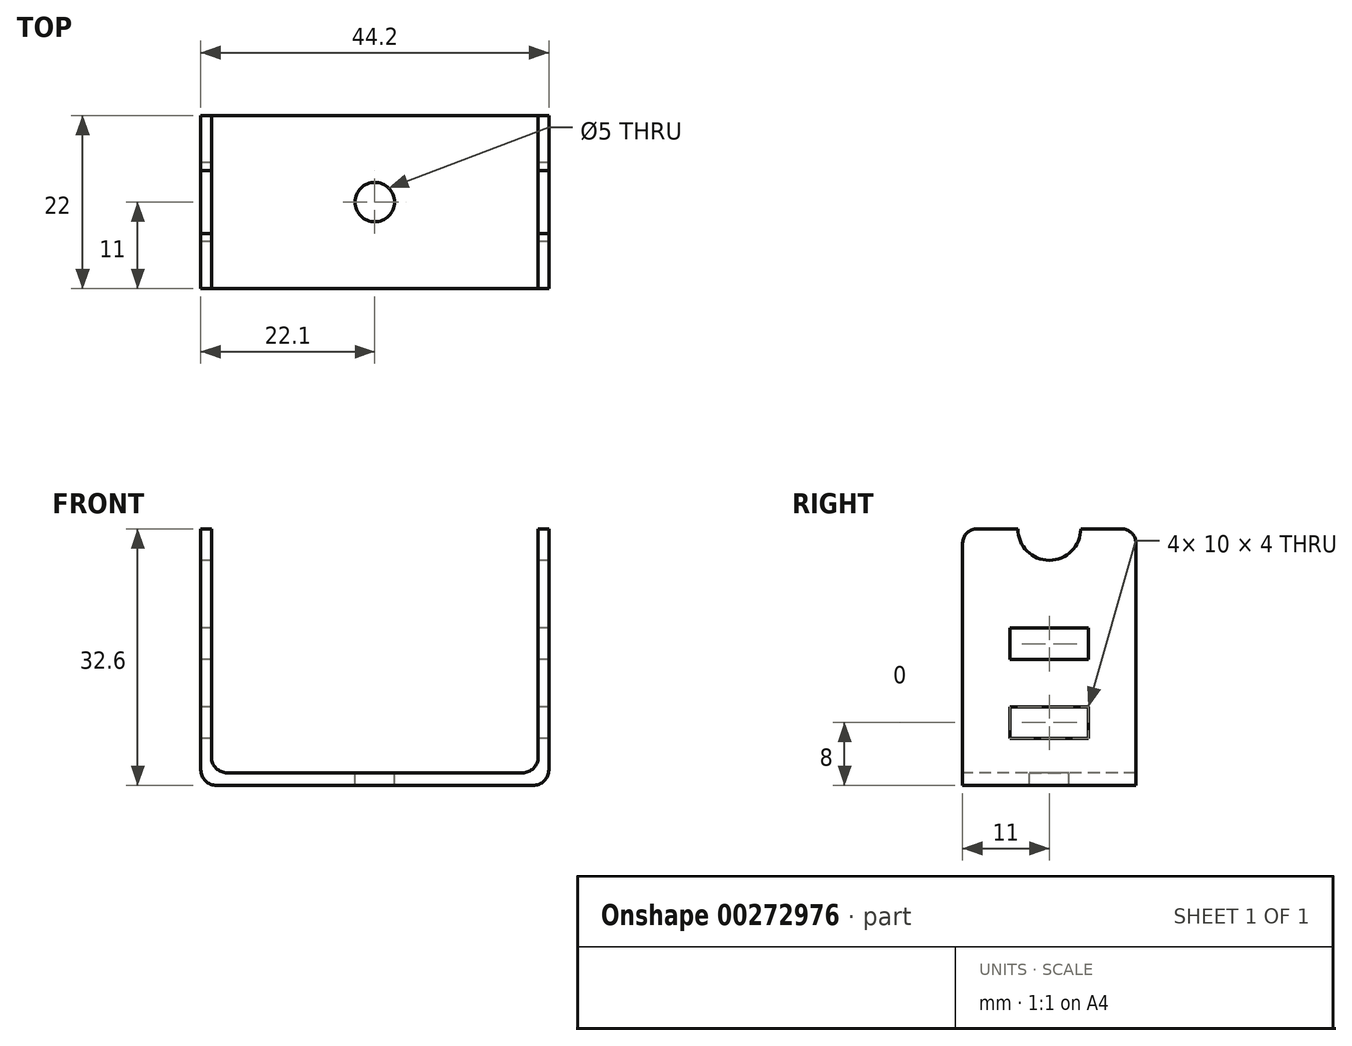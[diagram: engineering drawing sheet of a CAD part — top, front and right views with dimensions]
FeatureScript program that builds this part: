
annotation { "Feature Type Name" : "Feature", "Feature Type Description" : "" }
export const myFeature = defineFeature(function(context is Context, id is Id, definition is map)
    precondition{}
    {
        {
            var Q0;
            Q0=qCreatedBy(makeId("Right.planeOp"),FACE);
            var sketch = newSketch(context, id + "F0", { "sketchPlane" : qUnion([Q0])});
            skLineSegment(sketch, "E0.bottom", {"start": v(-11, 0) * mm, "end": v(11, 0) * mm});
            skLineSegment(sketch, "E0.top", {"start": v(-9.17, 32.6) * mm, "end": v(-4, 32.6) * mm});
            skLineSegment(sketch, "E0.left", {"start": v(-11, 0) * mm, "end": v(-11, 30.77) * mm});
            skLineSegment(sketch, "E0.right", {"start": v(11, 0) * mm, "end": v(11, 30.77) * mm});
            skLineSegment(sketch, "E1.bottom", {"start": v(-5, 10) * mm, "end": v(5, 10) * mm});
            skLineSegment(sketch, "E1.top", {"start": v(-5, 6) * mm, "end": v(5, 6) * mm});
            skLineSegment(sketch, "E1.left", {"start": v(-5, 10) * mm, "end": v(-5, 6) * mm});
            skLineSegment(sketch, "E1.right", {"start": v(5, 10) * mm, "end": v(5, 6) * mm});
            skLineSegment(sketch, "E2.0.1.0", {"start": v(-5, 16) * mm, "end": v(5, 16) * mm});
            skLineSegment(sketch, "E2.0.1.1", {"start": v(5, 20) * mm, "end": v(5, 16) * mm});
            skLineSegment(sketch, "E2.0.1.2", {"start": v(-5, 20) * mm, "end": v(5, 20) * mm});
            skLineSegment(sketch, "E2.0.1.3", {"start": v(-5, 20) * mm, "end": v(-5, 16) * mm});
            skLineSegment(sketch, "E2.direction1", {"start": v(-5, 6) * mm, "end": v(17, 6) * mm, "construction": true});
            skLineSegment(sketch, "E2.direction2", {"start": v(-5, 6) * mm, "end": v(-5, 16) * mm, "construction": true});
            skArc(sketch, "E3", {"start": v(-4, 32.6) * mm, "mid": v(0, 28.6) * mm, "end": v(4, 32.6) * mm});
            skLineSegment(sketch, "E4.trimOffspring", {"start": v(4, 32.6) * mm, "end": v(9.17, 32.6) * mm});
            skPoint(sketch, "E5.visualSharp", {"position": v(-11, 32.6) * mm});
            skArc(sketch, "E5.filletArc", {"start": v(-9.17, 32.6) * mm, "mid": v(-10.46, 32.06) * mm, "end": v(-11, 30.77) * mm});
            skPoint(sketch, "E6.visualSharp", {"position": v(11, 32.6) * mm});
            skArc(sketch, "E6.filletArc", {"start": v(11, 30.77) * mm, "mid": v(10.46, 32.06) * mm, "end": v(9.17, 32.6) * mm});
            skSolve(sketch);
        }
        {
            var Q0;
            Q0 = qSketchRegion(id + "F0", true);
            extrude(context, id + "F1", {"entities" : qUnion([Q0]), "endBound" : BoundingType.SYMMETRIC, "depth" : 44.2 * mm});
        }
        {
            var Q0;
            Q0=makeQuery(id+"F1.opExtrude","SWEPT_FACE",FACE,{"disambiguationData":[OSD([sQuery(id+"F0.wireOp",EDGE,"E0.top")])]});
            var sketch = newSketch(context, id + "F2", { "sketchPlane" : qUnion([Q0])});
            skLineSegment(sketch, "E7.bottom", {"start": v(-20.75, 21.18) * mm, "end": v(20.75, 21.18) * mm});
            skLineSegment(sketch, "E7.top", {"start": v(-20.75, -22.3) * mm, "end": v(20.75, -22.3) * mm});
            skLineSegment(sketch, "E7.left", {"start": v(-20.75, 21.18) * mm, "end": v(-20.75, -22.3) * mm});
            skLineSegment(sketch, "E7.right", {"start": v(20.75, 21.18) * mm, "end": v(20.75, -22.3) * mm});
            skSolve(sketch);
        }
        {
            var Q0;
            Q0 = qSketchRegion(id + "F2", true);
            extrude(context, id + "F3", {"entities" : qUnion([Q0]), "operationType" : NewBodyOperationType.REMOVE, "oppositeDirection" : true, "depth" : (32.5 - 1.5) * mm});
        }
        {
            var Q0;
            Q0=makeQuery(id+"F1.opExtrude","CAP_EDGE",EDGE,{"disambiguationData":[OSD([sQuery(id+"F0.wireOp",EDGE,"E0.bottom")])],"isStart":true});
            fillet(context, id + "F4", {"entities" : qUnion([Q0]), "radius" : 2 * mm, "tangentPropagation" : true, "allowEdgeOverflow" : false});
        }
        {
            var Q0;
            Q0=makeQuery(id+"F1.opExtrude","CAP_EDGE",EDGE,{"disambiguationData":[OSD([sQuery(id+"F0.wireOp",EDGE,"E0.bottom")])],"isStart":false});
            var Q1;
            Q1=makeQuery(id+"F3.boolean.opBoolean","COPY",EDGE,{"derivedFrom":makeQuery(id+"F3.opExtrude","CAP_EDGE",EDGE,{"disambiguationData":[OSD([sQuery(id+"F2.wireOp",EDGE,"E7.left")])],"isStart":false})});
            var Q2;
            Q2=makeQuery(id+"F3.boolean.opBoolean","COPY",EDGE,{"derivedFrom":makeQuery(id+"F3.opExtrude","CAP_EDGE",EDGE,{"disambiguationData":[OSD([sQuery(id+"F2.wireOp",EDGE,"E7.right")])],"isStart":false})});
            fillet(context, id + "F5", {"entities" : qUnion([Q0, Q1, Q2]), "radius" : 2 * mm, "tangentPropagation" : true, "allowEdgeOverflow" : false});
        }
        {
            var Q0;
            Q0=makeQuery(id+"F3.boolean.opBoolean","COPY",FACE,{"derivedFrom":makeQuery(id+"F3.opExtrude","CAP_FACE",FACE,{"disambiguationData":[OSD([sQuery(id+"F2.wireOp",EDGE,"E7.bottom"),sQuery(id+"F2.wireOp",EDGE,"E7.top"),sQuery(id+"F2.wireOp",EDGE,"E7.left"),sQuery(id+"F2.wireOp",EDGE,"E7.right")])],"isStart":false})});
            var sketch = newSketch(context, id + "F6", { "sketchPlane" : qUnion([Q0])});
            skCircle(sketch, "E8", {"center": v(0, 0) * mm, "radius": 2.5 * mm});
            skSolve(sketch);
        }
        {
            var Q0;
            Q0 = qSketchRegion(id + "F6", true);
            extrude(context, id + "F7", {"entities" : qUnion([Q0]), "operationType" : NewBodyOperationType.REMOVE, "oppositeDirection" : true, "depth" : 25 * mm});
        }
    });
